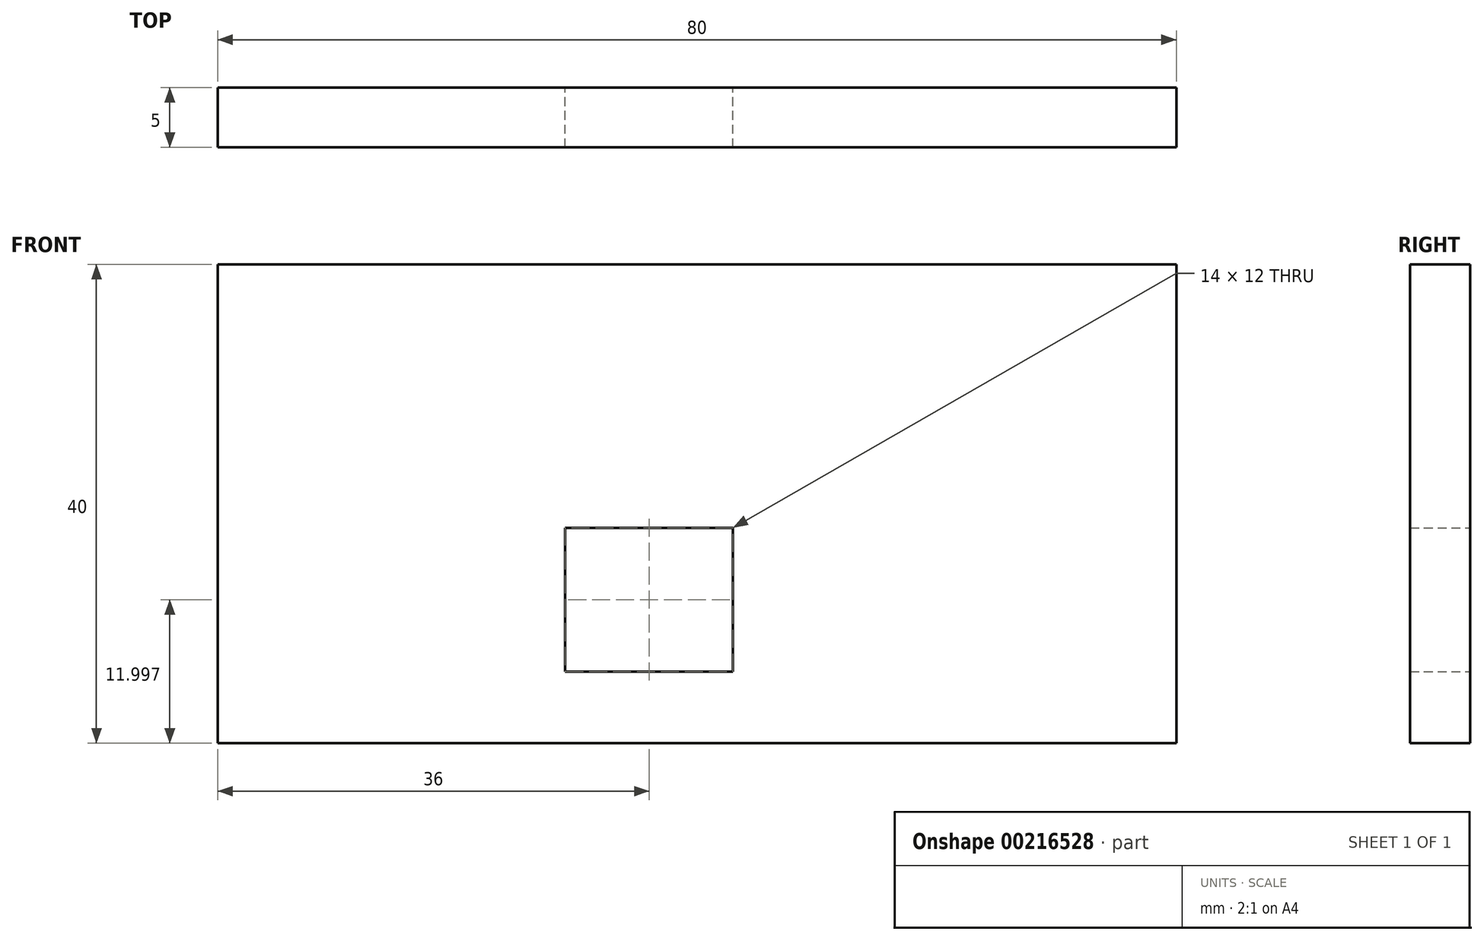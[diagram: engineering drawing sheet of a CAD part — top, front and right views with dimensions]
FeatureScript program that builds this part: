
annotation { "Feature Type Name" : "Feature", "Feature Type Description" : "" }
export const myFeature = defineFeature(function(context is Context, id is Id, definition is map)
    precondition{}
    {
        {
            var Q0;
            Q0=qCreatedBy(makeId("Front.planeOp"),FACE);
            var sketch = newSketch(context, id + "F0", { "sketchPlane" : qUnion([Q0])});
            skLineSegment(sketch, "E0.bottom", {"start": v(-40, 15.27) * mm, "end": v(40, 15.27) * mm});
            skLineSegment(sketch, "E0.top", {"start": v(-40, -24.73) * mm, "end": v(40, -24.73) * mm});
            skLineSegment(sketch, "E0.left", {"start": v(-40, 15.27) * mm, "end": v(-40, -24.73) * mm});
            skLineSegment(sketch, "E0.right", {"start": v(40, 15.27) * mm, "end": v(40, -24.73) * mm});
            skLineSegment(sketch, "E1.bottom", {"start": v(-11, -6.73) * mm, "end": v(3, -6.73) * mm});
            skLineSegment(sketch, "E1.top", {"start": v(-11, -18.73) * mm, "end": v(3, -18.73) * mm});
            skLineSegment(sketch, "E1.left", {"start": v(-11, -6.73) * mm, "end": v(-11, -18.73) * mm});
            skLineSegment(sketch, "E1.right", {"start": v(3, -6.73) * mm, "end": v(3, -18.73) * mm});
            skSolve(sketch);
        }
        {
            var Q0;
            Q0 = qSketchRegion(id + "F0", true);
            extrude(context, id + "F1", {"entities" : qUnion([Q0]), "depth" : 5 * mm});
        }
    });
